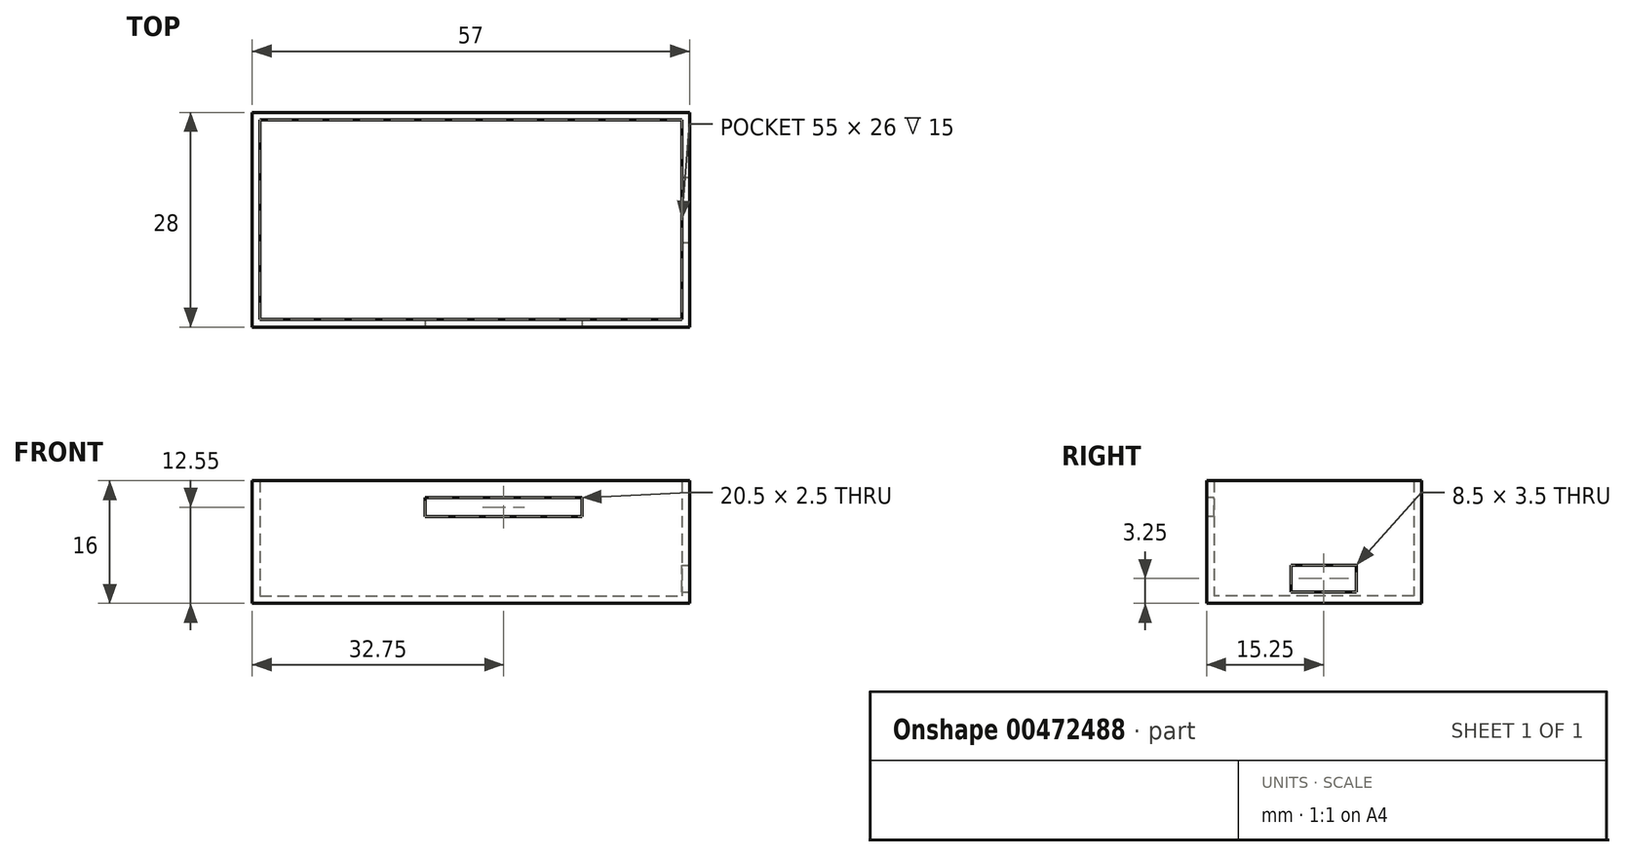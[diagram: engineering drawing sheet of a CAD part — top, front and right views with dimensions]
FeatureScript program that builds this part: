
annotation { "Feature Type Name" : "Feature", "Feature Type Description" : "" }
export const myFeature = defineFeature(function(context is Context, id is Id, definition is map)
    precondition{}
    {
        {
            var Q0;
            Q0=qCreatedBy(makeId("Top.planeOp"),FACE);
            var sketch = newSketch(context, id + "F0", { "sketchPlane" : qUnion([Q0])});
            skLineSegment(sketch, "E0.bottom", {"start": v(-28.5, 14) * mm, "end": v(28.5, 14) * mm});
            skLineSegment(sketch, "E0.top", {"start": v(-28.5, -14) * mm, "end": v(28.5, -14) * mm});
            skLineSegment(sketch, "E0.left", {"start": v(-28.5, 14) * mm, "end": v(-28.5, -14) * mm});
            skLineSegment(sketch, "E0.right", {"start": v(28.5, 14) * mm, "end": v(28.5, -14) * mm});
            skPoint(sketch, "E0.middle", {"position": v(0, 0) * mm});
            skSolve(sketch);
        }
        {
            var Q0;
            Q0 = qSketchRegion(id + "F0", true);
            extrude(context, id + "F1", {"entities" : qUnion([Q0]), "depth" : 16 * mm});
        }
        {
            var Q0;
            Q0=makeQuery(id+"F1.opExtrude","CAP_FACE",FACE,{"disambiguationData":[OSD([sQuery(id+"F0.wireOp",EDGE,"E0.bottom"),sQuery(id+"F0.wireOp",EDGE,"E0.top"),sQuery(id+"F0.wireOp",EDGE,"E0.left"),sQuery(id+"F0.wireOp",EDGE,"E0.right")])],"isStart":false});
            shell(context, id + "F2", {"entities" : qUnion([Q0]), "thickness" : 1 * mm});
        }
        {
            var Q0;
            Q0=makeQuery(id+"F1.opExtrude","SWEPT_FACE",FACE,{"disambiguationData":[OSD([sQuery(id+"F0.wireOp",EDGE,"E0.top")])]});
            var sketch = newSketch(context, id + "F3", { "sketchPlane" : qUnion([Q0])});
            skLineSegment(sketch, "E1.0", {"start": v(-28.5, 16) * mm, "end": v(28.5, 16) * mm});
            skLineSegment(sketch, "E2.bottom", {"start": v(-6, 13.8) * mm, "end": v(14.5, 13.8) * mm});
            skLineSegment(sketch, "E2.top", {"start": v(-6, 11.3) * mm, "end": v(14.5, 11.3) * mm});
            skLineSegment(sketch, "E2.left", {"start": v(-6, 13.8) * mm, "end": v(-6, 11.3) * mm});
            skLineSegment(sketch, "E2.right", {"start": v(14.5, 13.8) * mm, "end": v(14.5, 11.3) * mm});
            skSolve(sketch);
        }
        {
            var Q0;
            Q0=makeQuery(id+"F3.imprint","IMPRINT",FACE,{"disambiguationData":[TD([[makeQuery(id+"F3.imprint","IMPRINT",EDGE,{"derivedFrom":sQuery(id+"F3.wireOp",EDGE,"E2.bottom")}),-1.0]])]});
            extrude(context, id + "F4", {"entities" : qUnion([Q0]), "operationType" : NewBodyOperationType.REMOVE, "oppositeDirection" : true, "depth" : 3 * mm});
        }
        {
            var Q0;
            Q0=makeQuery(id+"F1.opExtrude","SWEPT_FACE",FACE,{"disambiguationData":[OSD([sQuery(id+"F0.wireOp",EDGE,"E0.right")])]});
            var sketch = newSketch(context, id + "F5", { "sketchPlane" : qUnion([Q0])});
            skLineSegment(sketch, "E3.bottom", {"start": v(-3, 1.5) * mm, "end": v(5.5, 1.5) * mm});
            skLineSegment(sketch, "E3.top", {"start": v(-3, 5) * mm, "end": v(5.5, 5) * mm});
            skLineSegment(sketch, "E3.left", {"start": v(-3, 1.5) * mm, "end": v(-3, 5) * mm});
            skLineSegment(sketch, "E3.right", {"start": v(5.5, 1.5) * mm, "end": v(5.5, 5) * mm});
            skSolve(sketch);
        }
        {
            var Q0;
            Q0=makeQuery(id+"F5.imprint","IMPRINT",FACE,{"disambiguationData":[TD([[makeQuery(id+"F5.imprint","IMPRINT",EDGE,{"derivedFrom":sQuery(id+"F5.wireOp",EDGE,"E3.bottom")}),1.0]])]});
            extrude(context, id + "F6", {"entities" : qUnion([Q0]), "operationType" : NewBodyOperationType.REMOVE, "oppositeDirection" : true, "depth" : 3 * mm});
        }
    });
